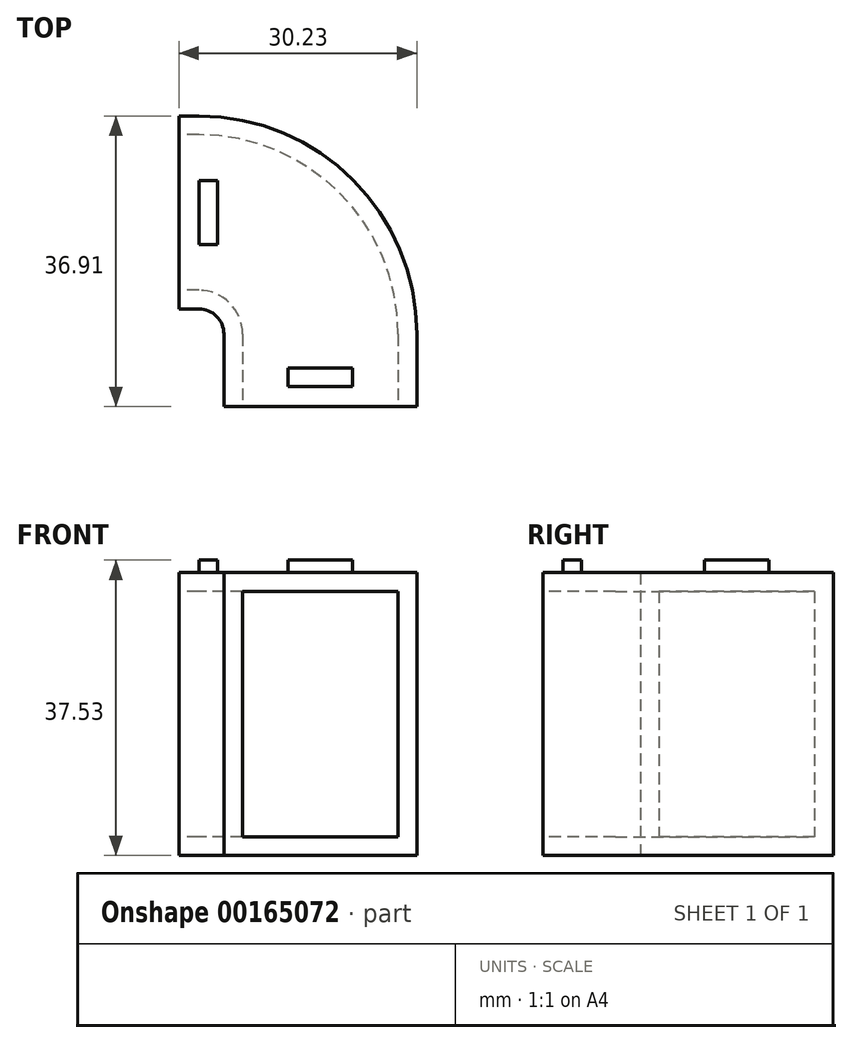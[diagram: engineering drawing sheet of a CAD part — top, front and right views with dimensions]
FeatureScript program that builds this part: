
annotation { "Feature Type Name" : "Feature", "Feature Type Description" : "" }
export const myFeature = defineFeature(function(context is Context, id is Id, definition is map)
    precondition{}
    {
        {
            var Q0;
            Q0=qCreatedBy(makeId("Top.planeOp"),FACE);
            var sketch = newSketch(context, id + "F0", { "sketchPlane" : qUnion([Q0])});
            skLineSegment(sketch, "E0.bottom", {"start": v(0, 0) * mm, "end": v(-2.54, 0) * mm});
            skLineSegment(sketch, "E0.top", {"start": v(0, -24.52) * mm, "end": v(-2.54, -24.52) * mm});
            skLineSegment(sketch, "E0.left", {"start": v(0, 0) * mm, "end": v(0, -24.52) * mm, "construction": true});
            skLineSegment(sketch, "E0.right", {"start": v(-2.54, 0) * mm, "end": v(-2.54, -24.52) * mm});
            skArc(sketch, "E1", {"start": v(3.18, -27.7) * mm, "mid": v(2.25, -25.45) * mm, "end": v(0, -24.52) * mm});
            skArc(sketch, "E2", {"start": v(27.7, -27.7) * mm, "mid": v(19.58, -8.11) * mm, "end": v(0, 0) * mm});
            skLineSegment(sketch, "E3.bottom", {"start": v(3.18, -27.7) * mm, "end": v(27.7, -27.7) * mm, "construction": true});
            skLineSegment(sketch, "E3.top", {"start": v(3.18, -36.9) * mm, "end": v(27.7, -36.9) * mm});
            skLineSegment(sketch, "E3.left", {"start": v(3.18, -27.7) * mm, "end": v(3.18, -36.9) * mm});
            skLineSegment(sketch, "E3.right", {"start": v(27.7, -27.7) * mm, "end": v(27.7, -36.9) * mm});
            skSolve(sketch);
        }
        {
            var Q0;
            Q0 = qSketchRegion(id + "F0", true);
            extrude(context, id + "F1", {"entities" : qUnion([Q0]), "depth" : 35.94 * mm});
        }
        {
            var Q0;
            Q0=makeQuery(id+"F1.opExtrude","SWEPT_FACE",FACE,{"disambiguationData":[OSD([sQuery(id+"F0.wireOp",EDGE,"E0.right")])]});
            shell(context, id + "F2", {"entities" : qUnion([Q0]), "thickness" : 2.38 * mm});
        }
        {
            var Q0;
            Q0=makeQuery(id+"F1.opExtrude","SWEPT_FACE",FACE,{"disambiguationData":[OSD([sQuery(id+"F0.wireOp",EDGE,"E3.top")])]});
            var sketch = newSketch(context, id + "F3", { "sketchPlane" : qUnion([Q0])});
            skLineSegment(sketch, "E4.bottom", {"start": v(3.18, 35.94) * mm, "end": v(5.56, 35.94) * mm, "construction": true});
            skLineSegment(sketch, "E4.top", {"start": v(3.18, 33.56) * mm, "end": v(5.56, 33.56) * mm, "construction": true});
            skLineSegment(sketch, "E4.left", {"start": v(3.18, 35.94) * mm, "end": v(3.18, 33.56) * mm, "construction": true});
            skLineSegment(sketch, "E4.right", {"start": v(5.56, 35.94) * mm, "end": v(5.56, 33.56) * mm, "construction": true});
            skLineSegment(sketch, "E5.bottom", {"start": v(27.7, 0) * mm, "end": v(25.31, 0) * mm, "construction": true});
            skLineSegment(sketch, "E5.top", {"start": v(27.7, 2.38) * mm, "end": v(25.31, 2.38) * mm, "construction": true});
            skLineSegment(sketch, "E5.left", {"start": v(27.7, 0) * mm, "end": v(27.7, 2.38) * mm, "construction": true});
            skLineSegment(sketch, "E5.right", {"start": v(25.31, 0) * mm, "end": v(25.31, 2.38) * mm, "construction": true});
            skLineSegment(sketch, "E6.bottom", {"start": v(5.56, 33.56) * mm, "end": v(25.31, 33.56) * mm});
            skLineSegment(sketch, "E6.top", {"start": v(5.56, 2.38) * mm, "end": v(25.31, 2.38) * mm});
            skLineSegment(sketch, "E6.left", {"start": v(5.56, 33.56) * mm, "end": v(5.56, 2.38) * mm});
            skLineSegment(sketch, "E6.right", {"start": v(25.31, 33.56) * mm, "end": v(25.31, 2.38) * mm});
            skSolve(sketch);
        }
        {
            var Q0;
            Q0 = qSketchRegion(id + "F3", true);
            extrude(context, id + "F4", {"entities" : qUnion([Q0]), "operationType" : NewBodyOperationType.REMOVE, "oppositeDirection" : true, "depth" : 2.38 * mm});
        }
        {
            var Q0;
            Q0=makeQuery(id+"F1.opExtrude","CAP_FACE",FACE,{"disambiguationData":[OSD([sQuery(id+"F0.wireOp",EDGE,"E0.bottom"),sQuery(id+"F0.wireOp",EDGE,"E0.top"),sQuery(id+"F0.wireOp",EDGE,"E0.right"),sQuery(id+"F0.wireOp",EDGE,"E1"),sQuery(id+"F0.wireOp",EDGE,"E2"),sQuery(id+"F0.wireOp",EDGE,"E3.top"),sQuery(id+"F0.wireOp",EDGE,"E3.left"),sQuery(id+"F0.wireOp",EDGE,"E3.right")])],"isStart":false});
            var sketch = newSketch(context, id + "F5", { "sketchPlane" : qUnion([Q0])});
            skLineSegment(sketch, "E7.bottom", {"start": v(0, -8.17) * mm, "end": v(2.38, -8.17) * mm});
            skLineSegment(sketch, "E7.top", {"start": v(0, -16.35) * mm, "end": v(2.38, -16.35) * mm});
            skLineSegment(sketch, "E7.left", {"start": v(0, -8.17) * mm, "end": v(0, -16.35) * mm});
            skLineSegment(sketch, "E7.right", {"start": v(2.38, -8.17) * mm, "end": v(2.38, -16.35) * mm});
            skLineSegment(sketch, "E8", {"start": v(0, 0) * mm, "end": v(0, -8.17) * mm, "construction": true});
            skLineSegment(sketch, "E9", {"start": v(0, -24.52) * mm, "end": v(0, -16.35) * mm, "construction": true});
            skLineSegment(sketch, "E10", {"start": v(15.43, -36.9) * mm, "end": v(15.43, -34.37) * mm, "construction": true});
            skLineSegment(sketch, "E11.bottom", {"start": v(11.35, -31.99) * mm, "end": v(19.52, -31.99) * mm});
            skLineSegment(sketch, "E11.top", {"start": v(11.35, -34.37) * mm, "end": v(19.52, -34.37) * mm});
            skLineSegment(sketch, "E11.left", {"start": v(11.35, -31.99) * mm, "end": v(11.35, -34.37) * mm});
            skLineSegment(sketch, "E11.right", {"start": v(19.52, -31.99) * mm, "end": v(19.52, -34.37) * mm});
            skSolve(sketch);
        }
        {
            var Q0;
            Q0 = qSketchRegion(id + "F5", true);
            extrude(context, id + "F6", {"entities" : qUnion([Q0]), "operationType" : NewBodyOperationType.ADD, "depth" : 1.59 * mm});
        }
    });
